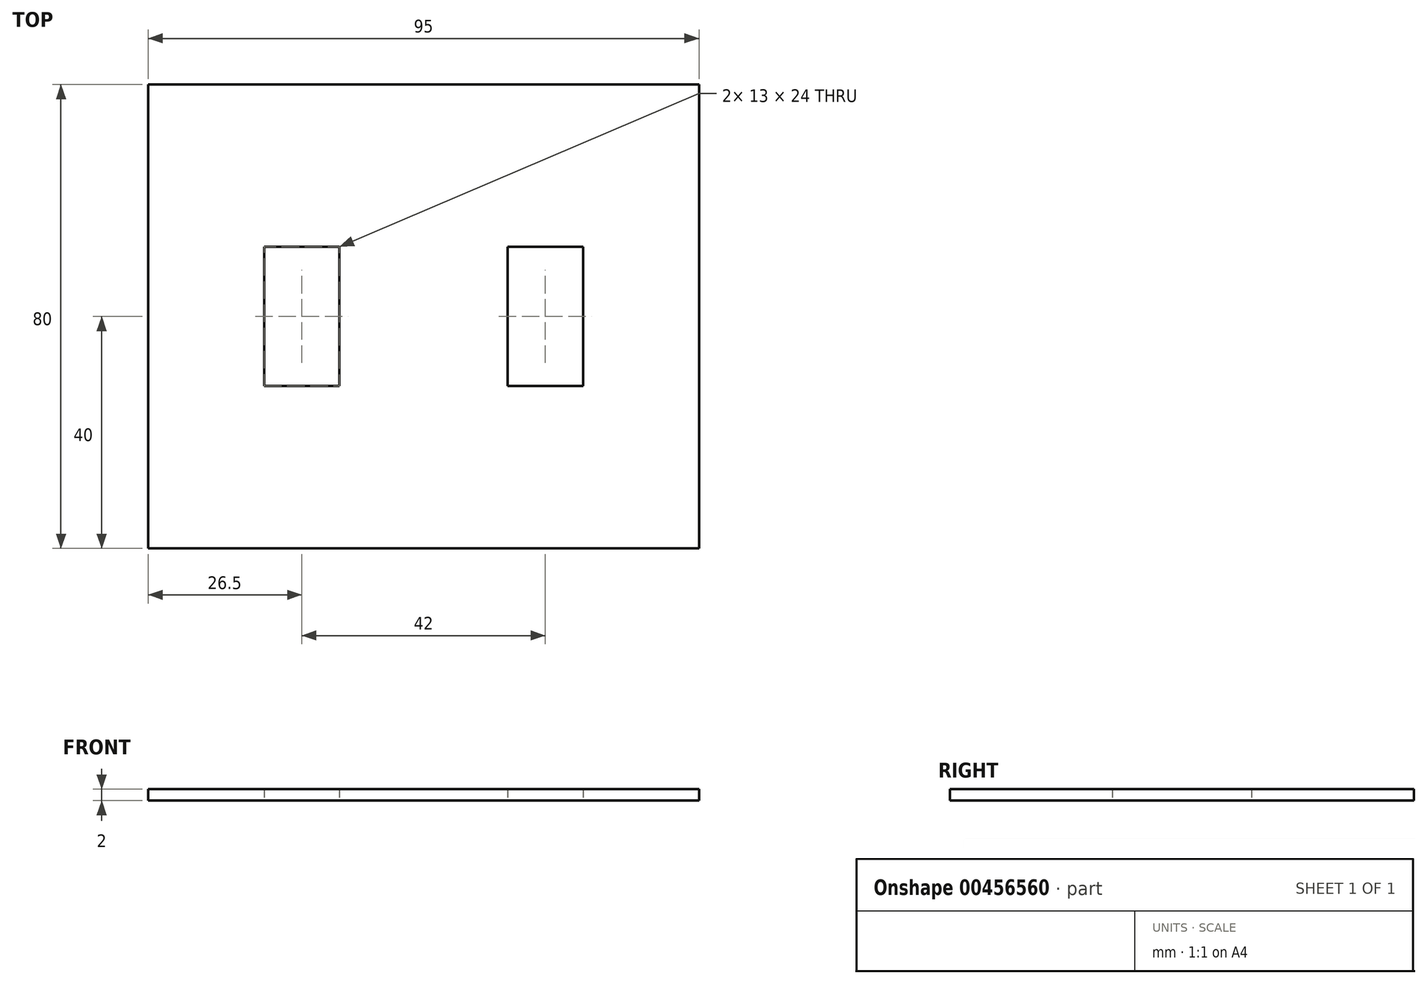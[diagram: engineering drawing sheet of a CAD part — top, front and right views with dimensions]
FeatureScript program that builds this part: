
annotation { "Feature Type Name" : "Feature", "Feature Type Description" : "" }
export const myFeature = defineFeature(function(context is Context, id is Id, definition is map)
    precondition{}
    {
        {
            var Q0;
            Q0=qCreatedBy(makeId("Top.planeOp"),FACE);
            var sketch = newSketch(context, id + "F0", { "sketchPlane" : qUnion([Q0])});
            skLineSegment(sketch, "E0.bottom", {"start": v(-47.5, -40) * mm, "end": v(47.5, -40) * mm});
            skLineSegment(sketch, "E0.top", {"start": v(-47.5, 40) * mm, "end": v(47.5, 40) * mm});
            skLineSegment(sketch, "E0.left", {"start": v(-47.5, -40) * mm, "end": v(-47.5, 40) * mm});
            skLineSegment(sketch, "E0.right", {"start": v(47.5, -40) * mm, "end": v(47.5, 40) * mm});
            skPoint(sketch, "E0.middle", {"position": v(0, 0) * mm});
            skLineSegment(sketch, "E1.bottom", {"start": v(-27.5, 12) * mm, "end": v(-14.5, 12) * mm});
            skLineSegment(sketch, "E1.top", {"start": v(-27.5, -12) * mm, "end": v(-14.5, -12) * mm});
            skLineSegment(sketch, "E1.left", {"start": v(-27.5, 12) * mm, "end": v(-27.5, -12) * mm});
            skLineSegment(sketch, "E1.right", {"start": v(-14.5, 12) * mm, "end": v(-14.5, -12) * mm});
            skLineSegment(sketch, "E2.bottom", {"start": v(14.5, 12) * mm, "end": v(27.5, 12) * mm});
            skLineSegment(sketch, "E2.top", {"start": v(14.5, -12) * mm, "end": v(27.5, -12) * mm});
            skLineSegment(sketch, "E2.left", {"start": v(14.5, 12) * mm, "end": v(14.5, -12) * mm});
            skLineSegment(sketch, "E2.right", {"start": v(27.5, 12) * mm, "end": v(27.5, -12) * mm});
            skSolve(sketch);
        }
        {
            var Q0;
            Q0=makeQuery(id+"F0.imprint","IMPRINT",FACE,{"disambiguationData":[TD([[makeQuery(id+"F0.imprint","IMPRINT",EDGE,{"derivedFrom":sQuery(id+"F0.wireOp",EDGE,"E0.bottom")}),1.0]])]});
            extrude(context, id + "F1", {"entities" : qUnion([Q0]), "depth" : 2 * mm});
        }
    });
